SOLIDWORKS PART (.sldprt)
format: sldprt  version: not decoded by parser v0  size: 1,612,800 bytes
history: native  units: mm
features: sketch x17, cut_extrude x9, extrude x4, plane x4, fillet x2, mirror x2, revolve x2, pattern_linear x2, material x1 + 1 further entry (+13 scaffold rows collapsed)
feature tree (57):
  scaffold x13  (default folders/planes/origin — collapsed)
  material  "Material <not specified>"
  "Design Table"
  sketch  "Sketch1"  dims[c1.D7=1.7018mm c1.D8=1.4478mm c1.D9=1.5875mm c1.D12=~3.217355mm c1.D13=0.2942mm c1.D14=0.254mm c1.D15=1.4478mm c1.D1=1.1938mm c1.D2=1.1938mm c1.D3=34.1884mm c1.D4=41.275mm c1.D5=8.7376mm c1.D6=4.7498mm c1.D10=~1.641398mm c1.D11=7.9756mm c2.D12=1.1938mm c2.D10=36.0426mm c3.D12=16.3322mm c3.D13=1.4224mm]
  extrude  "Extrude1"  Depth=711.2mm Length=711.2mm
  plane  "Plane1"  Offset=381mm
  sketch  "Sketch2"  dims[c1.D5=1.4478mm c1.D9=~1.267414mm c1.D10=1.2192mm c1.D11=1.2192mm c1.D12=~3.918466mm c1.D13=~3.918466mm c1.D15=1.5875mm c1.D18=~1.267414mm c1.D1=1.1938mm c1.D2=~2.687521mm c1.D3=~5.746635mm c1.D4=~0.884121mm c1.D6=~0.650638mm c2.D6=135.0deg c2.D7=~7.603089mm c2.D8=~27.132233mm c2.D9=~29.229431mm c2.D10=31.8516mm c2.D13=~41.363079mm c2.D14=~6.838891mm c3.D14=~38.423891deg c3.D16=~25.100233mm c3.D17=~2.951279mm c3.D19=3.4544mm c3.D20=~1.661599mm c3.D21=~1.268195mm c3.D1=1.1938mm c3.Length=711.2mm c3.D5=1.1938mm c3.D6=1.0mm c3.D7=5.0mm]
  plane  "Plane2"  Offset=762mm Travel=762mm
  sketch  "Sketch3"  dims[c1.D2=1.8288mm c1.D3=~1.822024mm c1.D5=1.8288mm c1.D6=~1.822024mm c1.D1=9.525mm c2.D2=~19.958679mm c2.D3=~26.006344mm c2.D4=~5.075387mm c2.D1=709.93mm c2.D5=1.1938mm c2.D6=1.0mm c2.D7=5.0mm]
  sketch  "Sketch4"  dims[D1=1.7018mm D2=16.002mm]
  cut_extrude  "Cut-Extrude1"  [1 undecoded]
  sketch  "Sketch5"  dims[D1=1.1938mm]
  extrude  "Extrude2"  Depth=6.9088mm
  fillet  "Fillet1"  Radius=0.508mm
  fillet  "Fillet2"  Radius=1.7018mm
  sketch  "Sketch6"  dims[c1.D1=6.4738mm c1.D2=4.8768mm c1.D3=2.4384mm c1.D5=~6.721523mm c1.D6=4.8768mm c2.D1=9.906mm c2.D3=~11.332591mm c2.D4=~11.332591mm c3.D3=10.4902mm c3.D4=12.7mm c3.D5=60.706mm c3.D6=111.506mm c3.D7=12.7mm]
  cut_extrude  "Cut-Extrude2"  [1 undecoded]
  sketch  "Sketch7"  dims[Cut A=191.135mm]
  cut_extrude  "Cut A"  [1 undecoded]
  sketch  "Sketch8"  dims[Cut A=191.135mm Cut B=283.21mm]
  cut_extrude  "Cut B"  [1 undecoded]
  sketch  "Sketch9"  dims[D2=4.8768mm D1=12.7mm Cut C=304.8mm]
  cut_extrude  "Cut C"  [1 undecoded]
  sketch  "Sketch10"  dims[c1.D1=4.8768mm c1.D2=2.4384mm c2.D1=8.89mm c2.Cut D=467.36mm]
  cut_extrude  "Cut D"  [1 undecoded]
  sketch  "Sketch11"  dims[c1.D1=4.8768mm c1.D2=4.8768mm c2.D1=8.89mm c2.Cut D=518.16mm c2.Cut E=559.435mm]
  cut_extrude  "Cut E"  [1 undecoded]
  sketch  "Sketch12"  dims[c1.D2=4.8768mm c1.D3=2.4384mm c1.D1=12.7mm c1.Cut C=319.913mm c1.Cut F=641.35mm c2.D3=~6.629179mm]
  cut_extrude  "Cut F"  [1 undecoded]
  sketch  "Sketch13"  dims[c1.D1=4.572mm c1.D2=4.572mm c1.D3=4.572mm c1.D4=~2.055992mm c1.D5=4.572mm c1.D6=2.286mm c1.D7=2.286mm c1.D8=2.286mm c1.D9=2.286mm c2.D2=12.7mm c2.D3=12.7mm c2.D4=18.288mm c2.D5=28.956mm c2.D6=16.002mm c2.D7=37.846mm c2.D8=13.716mm c3.D6=69.596mm c3.D8=9.652mm c3.D9=76.2mm c3.D10=~25.247838mm]
  cut_extrude  "Cut-Extrude9"  [1 undecoded]
  mirror  "Mirror1"
  plane  "Plane3"  Offset=12.7mm
  sketch  "Sketch14"
  revolve  "Revolve1"  Angle=360deg
  pattern_linear  "LPattern1"  Count1=14 Count2=1 Spacing1=25.4mm Spacing2=50mm
  sketch  "Sketch15"  dims[D1=0.762mm D2=0.762mm D3=0.762mm]
  extrude  "Extrude3"  Depth=336.55mm
  plane  "Plane4"  Offset=12.7mm
  sketch  "Sketch16"
  revolve  "Revolve2"  Angle=360deg
  pattern_linear  "LPattern2"  Count1=12 Count2=1 Spacing1=25.4mm Spacing2=50mm
  sketch  "Sketch17"  dims[D1=0.762mm D2=0.762mm D3=0.762mm]
  extrude  "Extrude4"  Depth=285.75mm
  mirror  "Mirror2"
decode coverage: 25 of 38 modeling features carry decoded parameters; 1 rows unclassified (native names shown)
note: ~ marks probable driven/reference dimensions
note: 9 parameter values undecoded
summary: no parameter record found for 9 features
note: suppression state not decoded; provenance and decode notes live in map.json
